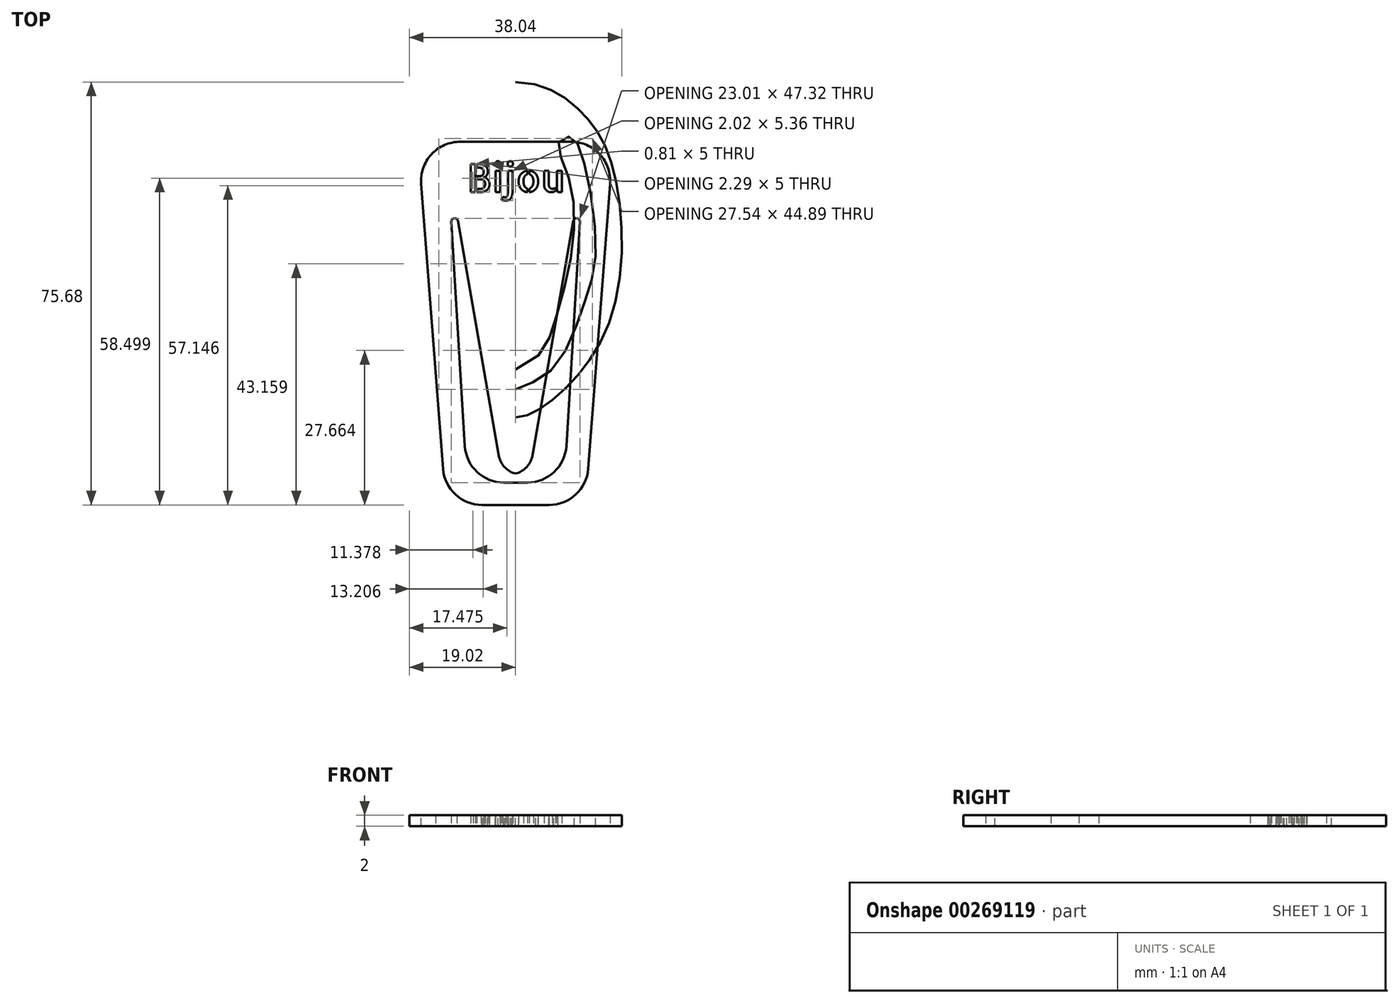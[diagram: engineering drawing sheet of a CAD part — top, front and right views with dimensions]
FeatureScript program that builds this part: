
annotation { "Feature Type Name" : "Feature", "Feature Type Description" : "" }
export const myFeature = defineFeature(function(context is Context, id is Id, definition is map)
    precondition{}
    {
        {
            var Q0;
            Q0=qCreatedBy(makeId("Top.planeOp"),FACE);
            var sketch = newSketch(context, id + "F0", { "sketchPlane" : qUnion([Q0])});
            skLineSegment(sketch, "E0.bottom", {"start": v(17.5, -30) * mm, "end": v(-17.5, -30) * mm, "construction": true});
            skLineSegment(sketch, "E0.top", {"start": v(17.5, 30) * mm, "end": v(-17.5, 30) * mm, "construction": true});
            skLineSegment(sketch, "E0.left", {"start": v(17.5, -30) * mm, "end": v(17.5, 30) * mm, "construction": true});
            skLineSegment(sketch, "E0.right", {"start": v(-17.5, -30) * mm, "end": v(-17.5, 30) * mm, "construction": true});
            skPoint(sketch, "E0.middle", {"position": v(0, 0) * mm});
            skFitSpline(sketch, "E1", {"points": [v(0, 30) * mm, v(-11.64, 24.78) * mm, v(-17.5, 14.3) * mm, v(-17.5, -10.79) * mm, v(-7.9, -25.77) * mm, v(0, -30) * mm], "startDerivative": vector(-82.87, 0) * mm, "endDerivative": vector(44.4, 0) * mm});
            skFitSpline(sketch, "E2.MirrorCS", {"points": [v(0, 30) * mm, v(11.64, 24.78) * mm, v(17.5, 14.3) * mm, v(17.5, -10.79) * mm, v(7.9, -25.77) * mm, v(0, -30) * mm], "startDerivative": vector(82.87, 0) * mm, "endDerivative": vector(-44.4, 0) * mm});
            skFitSpline(sketch, "E3", {"points": [v(0, -24.97) * mm, v(-6.55, -21.4) * mm, v(-12.13, -10.02) * mm, v(-14.34, 0) * mm, v(-11.8, 17.32) * mm, v(-9.76, 20.2) * mm, v(-7.72, 19.19) * mm, v(-9.42, 13.24) * mm, v(-10.1, 0) * mm, v(-6.55, -14.27) * mm, v(0, -21.4) * mm], "startDerivative": vector(-61.28, 26.15) * mm, "endDerivative": vector(133.24, -50.17) * mm});
            skFitSpline(sketch, "E4.MirrorCS", {"points": [v(0, -24.97) * mm, v(6.55, -21.4) * mm, v(12.13, -10.02) * mm, v(14.34, 0) * mm, v(11.8, 17.32) * mm, v(9.76, 20.2) * mm, v(7.72, 19.19) * mm, v(9.42, 13.24) * mm, v(10.1, 0) * mm, v(6.55, -14.27) * mm, v(0, -21.4) * mm], "startDerivative": vector(61.28, 26.15) * mm, "endDerivative": vector(-133.24, -50.17) * mm});
            skSolve(sketch);
        }
        {
            var Q0;
            Q0=makeQuery(id+"F0.imprint","IMPRINT",FACE,{"disambiguationData":[TD([[makeQuery(id+"F0.imprint","IMPRINT",EDGE,{"derivedFrom":sQuery(id+"F0.wireOp",EDGE,"E1")}),1.0]])]});
            extrude(context, id + "F1", {"entities" : qUnion([Q0]), "depth" : 2 * mm});
        }
        {
            var Q0;
            Q0=qCreatedBy(makeId("Top.planeOp"),FACE);
            var sketch = newSketch(context, id + "F2", { "sketchPlane" : qUnion([Q0])});
            skLineSegment(sketch, "E5", {"start": v(-17.5, 19.32) * mm, "end": v(-12.5, -45.68) * mm});
            skLineSegment(sketch, "E6.MirrorCS", {"start": v(17.5, 19.32) * mm, "end": v(12.5, -45.68) * mm});
            skLineSegment(sketch, "E7.1", {"start": v(-12.12, 15.32) * mm, "end": v(-8.7, -41.68) * mm});
            skLineSegment(sketch, "E7.2", {"start": v(-8.7, -41.68) * mm, "end": v(0, -41.68) * mm});
            skLineSegment(sketch, "E7.4", {"start": v(8.7, -41.68) * mm, "end": v(0, -41.68) * mm});
            skLineSegment(sketch, "E7.5", {"start": v(12.12, 15.32) * mm, "end": v(8.7, -41.68) * mm});
            skLineSegment(sketch, "E8", {"start": v(-12.12, 15.32) * mm, "end": v(-2.41, -40.18) * mm});
            skLineSegment(sketch, "E9.MirrorCS", {"start": v(12.12, 15.32) * mm, "end": v(2.41, -40.18) * mm});
            skText(sketch, "E10", { "text": "Bijou", "fontName": "AllertaStencil-Regular.ttf"});
            skLineSegment(sketch, "E11", {"start": v(-17.5, 19.32) * mm, "end": v(17.5, 19.32) * mm});
            skLineSegment(sketch, "E12", {"start": v(-12.5, -45.68) * mm, "end": v(12.5, -45.68) * mm});
            skLineSegment(sketch, "E13", {"start": v(-2.41, -40.18) * mm, "end": v(2.41, -40.18) * mm});
            const initialGuessF2  = {"E10": [-0.0087, 0.01032, 1, 0, 0.005]};
            skSetInitialGuess(sketch, initialGuessF2);
            skSolve(sketch);
        }
        {
            var Q0;
            Q0=makeQuery(id+"F2.imprint","IMPRINT",FACE,{"disambiguationData":[TD([[makeQuery(id+"F2.imprint","IMPRINT",EDGE,{"derivedFrom":sQuery(id+"F2.wireOp",EDGE,"pQgjq1LY-v7vb-70A7-Q3rA-JIM9d0O27qwe")}),1.0]])]});
            var Q1;
            Q1=makeQuery(id+"F2.imprint","IMPRINT",FACE,{"disambiguationData":[TD([[makeQuery(id+"F2.imprint","IMPRINT",EDGE,{"derivedFrom":sQuery(id+"F2.wireOp",EDGE,"E5")}),1.0]])]});
            extrude(context, id + "F3", {"entities" : qUnion([Q0, Q1]), "depth" : 2 * mm});
        }
        {
            var Q0;
            Q0=makeQuery(id+"F3.opExtrude","SWEPT_EDGE",EDGE,{"disambiguationData":[OSD([sQuery(id+"F2.wireOp",EDGE,"89772e7d-c365-46ac-9157-cfbe93683eb20.MirrorCS"),sQuery(id+"F2.wireOp",EDGE,"E6.MirrorCS")])]});
            var Q1;
            Q1=makeQuery(id+"F3.opExtrude","SWEPT_EDGE",EDGE,{"disambiguationData":[OSD([sQuery(id+"F2.wireOp",EDGE,"E5"),sQuery(id+"F2.wireOp",EDGE,"FlY1c6Dj-KE4i-gDru-A19Z-2DT1KuJbSgJd")])]});
            var Q2;
            Q2=makeQuery(id+"F3.opExtrude","SWEPT_EDGE",EDGE,{"disambiguationData":[OSD([sQuery(id+"F2.wireOp",EDGE,"E6.MirrorCS"),sQuery(id+"F2.wireOp",EDGE,"89772e7d-c365-46ac-9157-cfbe93683eb22.MirrorCS")])]});
            var Q3;
            Q3=makeQuery(id+"F3.opExtrude","SWEPT_EDGE",EDGE,{"disambiguationData":[OSD([sQuery(id+"F2.wireOp",EDGE,"pQgjq1LY-v7vb-70A7-Q3rA-JIM9d0O27qwe"),sQuery(id+"F2.wireOp",EDGE,"E5")])]});
            var Q4;
            Q4=makeQuery(id+"F3.opExtrude","SWEPT_EDGE",EDGE,{"disambiguationData":[OSD([sQuery(id+"F2.wireOp",EDGE,"E7.1"),sQuery(id+"F2.wireOp",EDGE,"E7.2")])]});
            var Q5;
            Q5=makeQuery(id+"F3.opExtrude","SWEPT_EDGE",EDGE,{"disambiguationData":[OSD([sQuery(id+"F2.wireOp",EDGE,"E7.4"),sQuery(id+"F2.wireOp",EDGE,"E7.5")])]});
            fillet(context, id + "F4", {"entities" : qUnion([Q0, Q1, Q2, Q3, Q4, Q5]), "radius" : 7 * mm, "tangentPropagation" : true, "allowEdgeOverflow" : false});
        }
        {
            var Q0;
            Q0=makeQuery(id+"F3.opExtrude","SWEPT_EDGE",EDGE,{"disambiguationData":[OSD([sQuery(id+"F2.wireOp",EDGE,"E7.1"),sQuery(id+"F2.wireOp",EDGE,"E8")])]});
            var Q1;
            Q1=makeQuery(id+"F3.opExtrude","SWEPT_EDGE",EDGE,{"disambiguationData":[OSD([sQuery(id+"F2.wireOp",EDGE,"E7.5"),sQuery(id+"F2.wireOp",EDGE,"E9.MirrorCS")])]});
            fillet(context, id + "F5", {"entities" : qUnion([Q0, Q1]), "radius" : 0.58 * mm, "tangentPropagation" : true, "allowEdgeOverflow" : false});
        }
        {
            var Q0;
            Q0=makeQuery(id+"F3.opExtrude","SWEPT_EDGE",EDGE,{"disambiguationData":[OSD([sQuery(id+"F2.wireOp",EDGE,"E9.MirrorCS"),sQuery(id+"F2.wireOp",EDGE,"7c4b9211-a30e-45c1-9c28-c942d3a7dfb10.MirrorCS")])]});
            var Q1;
            Q1=makeQuery(id+"F3.opExtrude","SWEPT_EDGE",EDGE,{"disambiguationData":[OSD([sQuery(id+"F2.wireOp",EDGE,"E8"),sQuery(id+"F2.wireOp",EDGE,"5WRu3LAk-ik1L-2j0v-NvGB-Ujjt8RKa559j")])]});
            fillet(context, id + "F6", {"entities" : qUnion([Q0, Q1]), "radius" : 4 * mm, "tangentPropagation" : true, "allowEdgeOverflow" : false});
        }
    });
